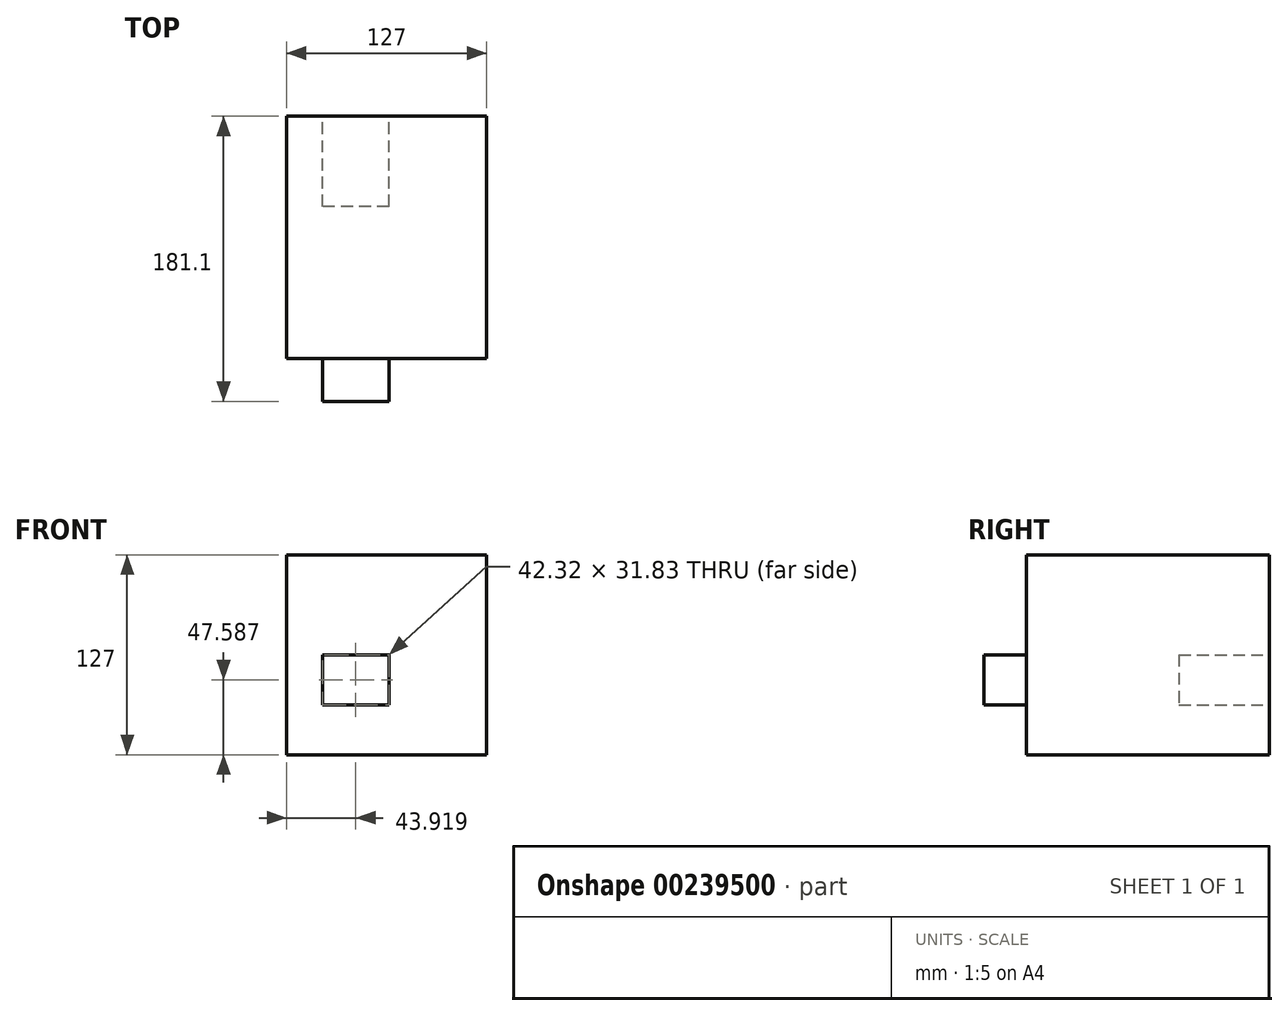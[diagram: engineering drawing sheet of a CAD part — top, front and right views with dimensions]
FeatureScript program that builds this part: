
annotation { "Feature Type Name" : "Feature", "Feature Type Description" : "" }
export const myFeature = defineFeature(function(context is Context, id is Id, definition is map)
    precondition{}
    {
        {
            var Q0;
            Q0=qCreatedBy(makeId("Front.planeOp"),FACE);
            var sketch = newSketch(context, id + "F0", { "sketchPlane" : qUnion([Q0])});
            skLineSegment(sketch, "E0.bottom", {"start": v(63.5, 63.5) * mm, "end": v(-63.5, 63.5) * mm});
            skLineSegment(sketch, "E0.top", {"start": v(63.5, -63.5) * mm, "end": v(-63.5, -63.5) * mm});
            skLineSegment(sketch, "E0.left", {"start": v(63.5, 63.5) * mm, "end": v(63.5, -63.5) * mm});
            skLineSegment(sketch, "E0.right", {"start": v(-63.5, 63.5) * mm, "end": v(-63.5, -63.5) * mm});
            skPoint(sketch, "E0.middle", {"position": v(0, 0) * mm});
            skSolve(sketch);
        }
        {
            var Q0;
            Q0 = qSketchRegion(id + "F0", true);
            extrude(context, id + "F1", {"entities" : qUnion([Q0]), "endBound" : BoundingType.SYMMETRIC, "depth" : 127 * mm});
        }
        {
            var Q0;
            Q0=makeQuery(id+"F1.opExtrude","CAP_FACE",FACE,{"disambiguationData":[OSD([sQuery(id+"F0.wireOp",EDGE,"E0.bottom"),sQuery(id+"F0.wireOp",EDGE,"E0.top"),sQuery(id+"F0.wireOp",EDGE,"E0.left"),sQuery(id+"F0.wireOp",EDGE,"E0.right")])],"isStart":false});
            var sketch = newSketch(context, id + "F2", { "sketchPlane" : qUnion([Q0])});
            skLineSegment(sketch, "E1.bottom", {"start": v(1.58, 0) * mm, "end": v(-40.74, 0) * mm});
            skLineSegment(sketch, "E1.top", {"start": v(1.58, -31.83) * mm, "end": v(-40.74, -31.83) * mm});
            skLineSegment(sketch, "E1.left", {"start": v(1.58, 0) * mm, "end": v(1.58, -31.83) * mm});
            skLineSegment(sketch, "E1.right", {"start": v(-40.74, 0) * mm, "end": v(-40.74, -31.83) * mm});
            skSolve(sketch);
        }
        {
            var Q0;
            Q0 = qSketchRegion(id + "F2", true);
            extrude(context, id + "F3", {"entities" : qUnion([Q0]), "operationType" : NewBodyOperationType.REMOVE, "depth" : 25.4 * mm});
        }
        {
            var Q0;
            Q0 = qSketchRegion(id + "F2", true);
            var Q1;
            Q1=makeQuery(id+"F1.opExtrude","CAP_FACE",FACE,{"disambiguationData":[OSD([sQuery(id+"F0.wireOp",EDGE,"E0.bottom"),sQuery(id+"F0.wireOp",EDGE,"E0.top"),sQuery(id+"F0.wireOp",EDGE,"E0.left"),sQuery(id+"F0.wireOp",EDGE,"E0.right")])],"isStart":true});
            extrude(context, id + "F4", {"entities" : qUnion([Q0, Q1]), "operationType" : NewBodyOperationType.ADD, "endBound" : BoundingType.SYMMETRIC, "oppositeDirection" : true, "depth" : 54.1 * mm});
        }
        {
            var Q0;
            Q0=makeQuery(id+"F4.opExtrude","CAP_FACE",FACE,{"disambiguationData":[OSD([sQuery(id+"F0.wireOp",EDGE,"E0.bottom"),sQuery(id+"F0.wireOp",EDGE,"E0.top"),sQuery(id+"F0.wireOp",EDGE,"E0.left"),sQuery(id+"F0.wireOp",EDGE,"E0.right")])],"isStart":false});
            var sketch = newSketch(context, id + "F5", { "sketchPlane" : qUnion([Q0])});
            skLineSegment(sketch, "E2.0", {"start": v(-1.58, 0) * mm, "end": v(40.74, 0) * mm});
            skLineSegment(sketch, "E3.0", {"start": v(-1.58, 0) * mm, "end": v(-1.58, -31.83) * mm});
            skLineSegment(sketch, "E4.0", {"start": v(-1.58, -31.83) * mm, "end": v(40.74, -31.83) * mm});
            skLineSegment(sketch, "E5.0", {"start": v(40.74, 0) * mm, "end": v(40.74, -31.83) * mm});
            skSolve(sketch);
        }
        {
            var Q0;
            Q0=makeQuery(id+"F5.imprint","IMPRINT",FACE,{"disambiguationData":[TD([[makeQuery(id+"F5.imprint","IMPRINT",EDGE,{"derivedFrom":sQuery(id+"F5.wireOp",EDGE,"E2.0")}),-1.0]])]});
            var Q1;
            Q1=sQuery(id+"F5.wireOp",EDGE,"E2.0");
            var Q2;
            Q2=sQuery(id+"F5.wireOp",EDGE,"E3.0");
            var Q3;
            Q3=sQuery(id+"F5.wireOp",EDGE,"E4.0");
            var Q4;
            Q4=sQuery(id+"F5.wireOp",EDGE,"E5.0");
            extrude(context, id + "F6", {"entities" : qUnion([Q0]), "operationType" : NewBodyOperationType.REMOVE, "surfaceEntities" : qUnion([Q1, Q2, Q3, Q4]), "endBound" : BoundingType.SYMMETRIC, "oppositeDirection" : true, "depth" : 114.8 * mm});
        }
    });
